# Revit family: Sefaira_Fixed
name_source: partatom
category: Windows
revit_build: Autodesk Revit Architecture 2014 (Build: 20130308_1515(x64)
units: mm (PartAtom-declared; Revit-internal decimal feet)

## types (9) — shared parameters
Analytic Construction = 1/8 in Pilkington single glazing
Assembly Code = B2020100
Construction Type Id = GSP4R
Glass Pane Material = Glass
Heat Transfer Coefficient (U) = 0.6496 BTU/(h·ft²·°F)
Sash Material = Sash
Solar Heat Gain Coefficient = 0.78
Thermal Resistance (R) = 1.5394 (h·ft²·°F)/BTU
Visual Light Transmittance = 0.9
Wall Closure = By host

## per-type parameters (varying)
| type | Default Sill Height | Height | Width |
| 36" x 48" | 3' - 0" | 6' - 0" | 2' - 0" |
| 24" x 48" | 3' - 0" | 6' - 0" | 2' - 0" |
| 24" x 24" | 3' - 0" | 2' - 0" | 2' - 0" |
| 16" x 24" | 3' - 0" | 2' - 0" | 1' - 4" |
| 16" x 48" | 3' - 0" | 4' - 0" | 1' - 4" |
| 16" x 72" | 1' - 0" | 6' - 0" | 1' - 4" |
| 24" x 72" | 1' - 0" | 6' - 0" | 2' - 0" |
| 36" x 24" | 3' - 0" | 2' - 0" | 3' - 0" |
| 36" x 72" | 1' - 0" | 6' - 0" | 3' - 0" |

## geometry (parser evidence)
native form markers: Blend x2, Sweep x2
no freeform markers — native parametric forms only
